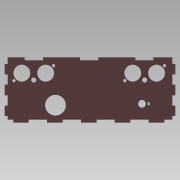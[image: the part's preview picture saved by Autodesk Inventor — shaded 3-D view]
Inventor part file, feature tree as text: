
AUTODESK INVENTOR PART (.ipt)
format: ipt  version: 2015 SP1 (Build 190203100, 203)  size: 195,584 bytes
history: native  units: mm
features: extrude x1, sketch x1
ambient origin geometry x8: Origin, YZ Plane, XZ Plane, XY Plane, X Axis, Y Axis, Z Axis, Center Point
bodies: Solid1 (feature_tree)
feature tree (2):
  extrude  "Extrusion1"  Depth=15.0mm
  sketch  "Sketch1"  dims[d2=20.0mm d4=15.0mm d5=3.0mm d8=30.0mm d10=32.5mm d11=30.0mm d13=32.5mm d16=1.5mm d17=3.0mm d18=10.0mm d19=20.0mm d21=20.0mm d22=20.0mm d24=20.0mm d27=3.0mm d28=0.0mm]
